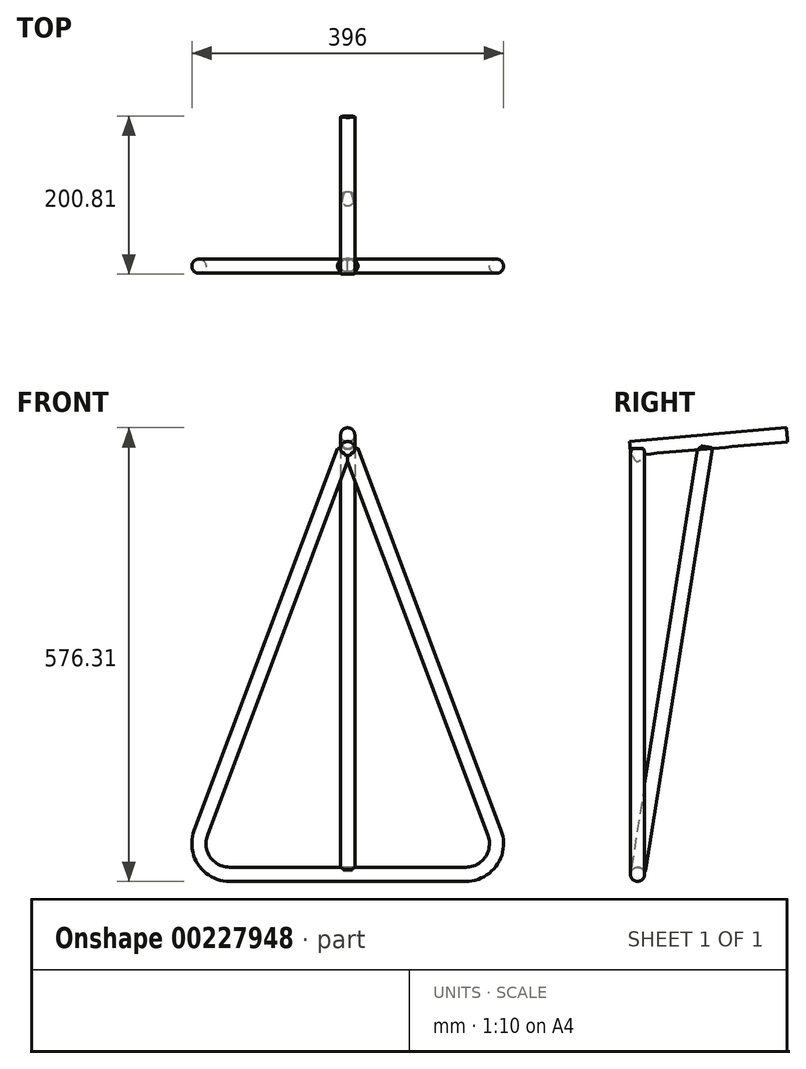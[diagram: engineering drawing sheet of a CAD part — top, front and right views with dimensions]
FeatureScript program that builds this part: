
annotation { "Feature Type Name" : "Feature", "Feature Type Description" : "" }
export const myFeature = defineFeature(function(context is Context, id is Id, definition is map)
    precondition{}
    {
        {
            var Q0;
            Q0=qCreatedBy(makeId("Front.planeOp"),FACE);
            var sketch = newSketch(context, id + "F0", { "sketchPlane" : qUnion([Q0]), "disableImprinting" : false});
            skCircle(sketch, "E0", {"center": v(-150, 0) * mm, "radius": 30 * mm});
            skLineSegment(sketch, "E1", {"start": v(0, -284.41) * mm, "end": v(0, 543.87) * mm, "construction": true});
            skLineSegment(sketch, "E2", {"start": v(-150, -30) * mm, "end": v(150, -30) * mm});
            skCircle(sketch, "E3.MirrorC", {"center": v(150, 0) * mm, "radius": 30 * mm});
            skLineSegment(sketch, "E4", {"start": v(0, 485.37) * mm, "end": v(-178.09, 10.54) * mm});
            skLineSegment(sketch, "E5.MirrorCS", {"start": v(0, 485.37) * mm, "end": v(178.09, 10.54) * mm});
            skLineSegment(sketch, "E6.0", {"start": v(0, 511) * mm, "end": v(-186.52, 13.7) * mm});
            skArc(sketch, "E7", {"start": v(-186.52, 13.7) * mm, "mid": v(-182.06, -22.21) * mm, "end": v(-150, -39) * mm});
            skLineSegment(sketch, "E8", {"start": v(-150, -39) * mm, "end": v(150, -39) * mm});
            skLineSegment(sketch, "E9.0", {"start": v(0, 511) * mm, "end": v(186.52, 13.7) * mm});
            skArc(sketch, "E10", {"start": v(150, -39) * mm, "mid": v(182.06, -22.21) * mm, "end": v(186.52, 13.7) * mm});
            skCircle(sketch, "E11", {"center": v(0, 485.37) * mm, "radius": 8 * mm});
            skCircle(sketch, "E12", {"center": v(0, 462.6) * mm, "radius": 8 * mm});
            skLineSegment(sketch, "E13", {"start": v(-117.06, -47) * mm, "end": v(146.74, -47) * mm});
            skSolve(sketch);
        }
        {
            var Q0;
            {var subQ6=sQuery(id+"F0.wireOp",EDGE,"E2");Q0=makeQuery(id+"F0.imprint","IMPRINT",FACE,{"disambiguationData":[TD([[makeQuery(id+"F0.imprint","IMPRINT",EDGE,{"derivedFrom":subQ6}),1.0]])]});}
            var sketch = newSketch(context, id + "F1", { "sketchPlane" : qUnion([Q0])});
            skLineSegment(sketch, "E14.0", {"start": v(0, 511) * mm, "end": v(-186.52, 13.7) * mm});
            skArc(sketch, "E14.1", {"start": v(-186.52, 13.7) * mm, "mid": v(-182.06, -22.21) * mm, "end": v(-150, -39) * mm});
            skLineSegment(sketch, "E14.2", {"start": v(-150, -39) * mm, "end": v(150, -39) * mm});
            skLineSegment(sketch, "E14.3", {"start": v(0, 511) * mm, "end": v(186.52, 13.7) * mm});
            skArc(sketch, "E14.4", {"start": v(150, -39) * mm, "mid": v(182.06, -22.21) * mm, "end": v(186.52, 13.7) * mm});
            skSolve(sketch);
        }
        {
            var Q0;
            Q0=sQuery(id+"F1.wireOp",VERTEX,"E14.4.start");
            var Q1;
            Q1=sQuery(id+"F1.wireOp",EDGE,"E14.2");
            cPlane(context, id + "F2", {"entities" : qUnion([Q0, Q1]), "cplaneType" : CPlaneType.CURVE_POINT, "offset" : 25 * mm, "width" : 150 * mm, "height" : 150 * mm});
        }
        {
            var Q0;
            Q0=qCreatedBy(id+"F2.planeOp",FACE);
            var sketch = newSketch(context, id + "F3", { "sketchPlane" : qUnion([Q0])});
            skCircle(sketch, "E15", {"center": v(0, -39) * mm, "radius": 9 * mm});
            skSolve(sketch);
        }
        {
            var Q0;
            Q0=makeQuery(id+"F3.imprint","IMPRINT",FACE,{"disambiguationData":[TD([[makeQuery(id+"F3.imprint","IMPRINT",EDGE,{"derivedFrom":sQuery(id+"F3.wireOp",EDGE,"E15")}),1.0]])]});
            var Q1;
            Q1=sQuery(id+"F1.wireOp",EDGE,"E14.2");
            var Q2;
            Q2=sQuery(id+"F1.wireOp",EDGE,"E14.4");
            var Q3;
            Q3=sQuery(id+"F1.wireOp",EDGE,"E14.1");
            var Q4;
            Q4=sQuery(id+"F1.wireOp",EDGE,"E14.0");
            var Q5;
            Q5=sQuery(id+"F1.wireOp",EDGE,"E14.3");
            sweep(context, id + "F4", {"profiles" : qUnion([Q0]), "path" : qUnion([Q1, Q2, Q3, Q4, Q5])});
        }
        {
            var Q0;
            Q0=qCreatedBy(makeId("Right.planeOp"),FACE);
            var sketch = newSketch(context, id + "F5", { "sketchPlane" : qUnion([Q0])});
            skLineSegment(sketch, "E16", {"start": v(0, 465.67) * mm, "end": v(144.94, 478.35) * mm});
            skSolve(sketch);
        }
        {
            var Q0;
            Q0=sQuery(id+"F0.wireOp",VERTEX,"E12.center");
            var Q1;
            Q1=sQuery(id+"F5.wireOp",EDGE,"E16");
            cPlane(context, id + "F6", {"entities" : qUnion([Q0, Q1]), "cplaneType" : CPlaneType.CURVE_POINT, "offset" : 25 * mm, "width" : 150 * mm, "height" : 150 * mm});
        }
        {
            var Q0;
            Q0=qCreatedBy(makeId("Front.planeOp"),FACE);
            var sketch = newSketch(context, id + "F7", { "sketchPlane" : qUnion([Q0])});
            skLineSegment(sketch, "E17.bottom", {"start": v(-89.17, 572.15) * mm, "end": v(122.26, 572.15) * mm});
            skLineSegment(sketch, "E17.top", {"start": v(-89.17, 502) * mm, "end": v(122.26, 502) * mm});
            skLineSegment(sketch, "E17.left", {"start": v(-89.17, 572.15) * mm, "end": v(-89.17, 502) * mm});
            skLineSegment(sketch, "E17.right", {"start": v(122.26, 572.15) * mm, "end": v(122.26, 502) * mm});
            skSolve(sketch);
        }
        {
            var Q0;
            Q0=makeQuery(id+"F7.imprint","IMPRINT",FACE,{"disambiguationData":[TD([[makeQuery(id+"F7.imprint","IMPRINT",EDGE,{"derivedFrom":sQuery(id+"F7.wireOp",EDGE,"E17.bottom")}),-1.0]])]});
            extrude(context, id + "F8", {"entities" : qUnion([Q0]), "operationType" : NewBodyOperationType.REMOVE, "oppositeDirection" : true, "depth" : 25 * mm, "symmetric" : true});
        }
        {
            var Q0;
            Q0=qCreatedBy(id+"F6.planeOp",FACE);
            var sketch = newSketch(context, id + "F9", { "sketchPlane" : qUnion([Q0])});
            skCircle(sketch, "E18", {"center": v(0, 500.82) * mm, "radius": 9 * mm});
            skSolve(sketch);
        }
        {
            var Q0;
            Q0=makeQuery(id+"F9.imprint","IMPRINT",FACE,{"disambiguationData":[TD([[makeQuery(id+"F9.imprint","IMPRINT",EDGE,{"derivedFrom":sQuery(id+"F9.wireOp",EDGE,"E18")}),1.0]])]});
            extrude(context, id + "F10", {"entities" : qUnion([Q0]), "operationType" : NewBodyOperationType.ADD, "depth" : 194 * mm, "hasSecondDirection" : true, "secondDirectionOppositeDirection" : true, "secondDirectionDepth" : 6 * mm});
        }
        {
            var Q0;
            Q0=qCreatedBy(makeId("Right.planeOp"),FACE);
            var sketch = newSketch(context, id + "F11", { "sketchPlane" : qUnion([Q0])});
            skLineSegment(sketch, "E19", {"start": v(-3.49, 502.43) * mm, "end": v(140.9, 515.06) * mm});
            skSolve(sketch);
        }
        {
            var Q0;
            Q0=qCreatedBy(makeId("Right.planeOp"),FACE);
            var sketch = newSketch(context, id + "F12", { "sketchPlane" : qUnion([Q0])});
            skLineSegment(sketch, "E20", {"start": v(0, -39) * mm, "end": v(87, 510.35) * mm});
            skSolve(sketch);
        }
        {
            var Q0;
            Q0=sQuery(id+"F0.wireOp",EDGE,"E8");
            cPoint(context, id + "F13", {"entities" : qUnion([Q0]), "parameter" : 0.5});
        }
        {
            var Q0;
            Q0=sQuery(id+"F12.wireOp",EDGE,"E20");
            var Q1;
            Q1=qCreatedBy(id+"F13",VERTEX);
            cPlane(context, id + "F14", {"entities" : qUnion([Q0, Q1]), "cplaneType" : CPlaneType.CURVE_POINT, "offset" : 25 * mm, "width" : 150 * mm, "height" : 150 * mm});
        }
        {
            var Q0;
            Q0=qCreatedBy(id+"F14.planeOp",FACE);
            var sketch = newSketch(context, id + "F15", { "sketchPlane" : qUnion([Q0])});
            skCircle(sketch, "E21", {"center": v(0, 6.1) * mm, "radius": 9 * mm});
            skSolve(sketch);
        }
        {
            var Q0;
            Q0=qSketchRegion(id+"F15",true);
            extrude(context, id + "F16", {"entities" : qUnion([Q0]), "depth" : 550 * mm, "hasSecondDirection" : true, "secondDirectionOppositeDirection" : false, "secondDirectionDepth" : 5 * mm});
        }
        {
            var Q0;
            Q0=makeQuery(id+"F4.opSweep","SWEPT_BODY",BODY,{"disambiguationData":[OSD([sQuery(id+"F1.wireOp",EDGE,"E14.1"),sQuery(id+"F3.wireOp",EDGE,"E15")])]});
            var Q1;
            Q1=makeQuery(id+"F16.opExtrude","SWEPT_BODY",BODY,{"disambiguationData":[OSD([sQuery(id+"F15.wireOp",EDGE,"E21")])]});
            booleanBodies(context, id + "F17", {"operationType" : BooleanOperationType.SUBTRACTION, "tools" : qUnion([Q0]), "targets" : qUnion([Q1]), "keepTools" : true});
        }
    });
